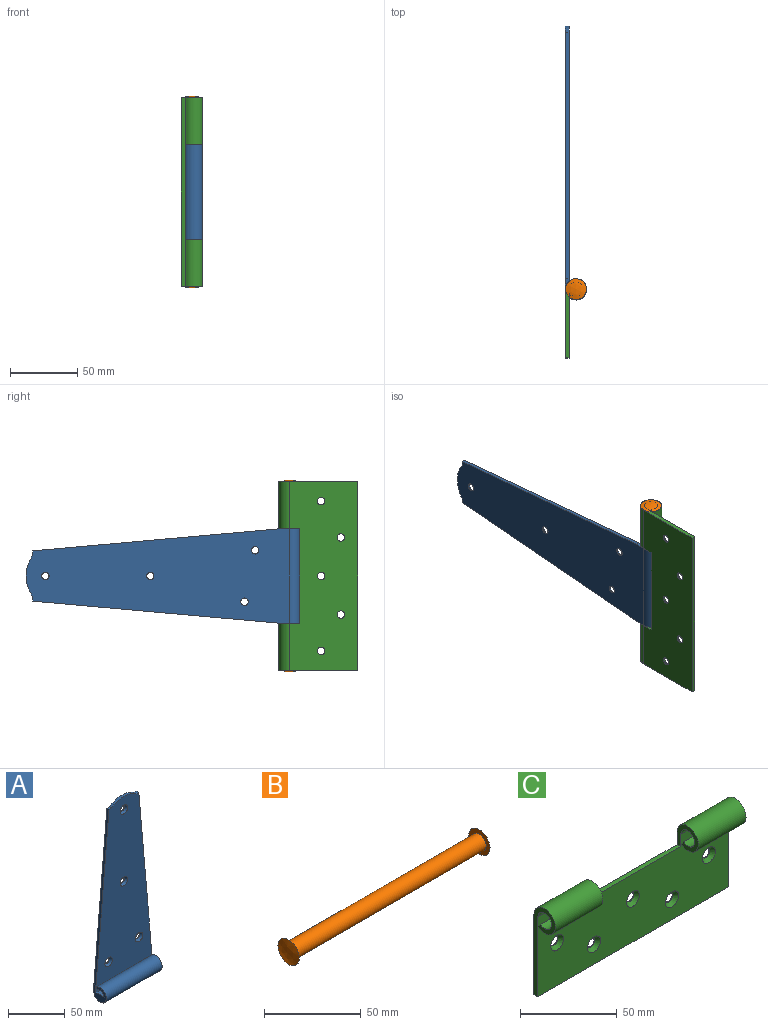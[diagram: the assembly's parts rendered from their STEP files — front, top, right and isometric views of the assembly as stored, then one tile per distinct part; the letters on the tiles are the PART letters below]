
ASSEMBLY  parts=3 mates=2
PART A: 21 faces, bbox 69.9x15.6x203.1 mm
  f0: cone r=4.76mm half-angle=41deg, axis (0,-1,0), area 72.6mm2, adj f7,f11
  f1: cone r=4.76mm half-angle=41deg, axis (0,-1,0), area 72.6mm2, adj f6,f11
  f2: cone r=4.76mm half-angle=41deg, axis (0,-1,0), area 72.6mm2, adj f5,f11
  f3: cone r=4.76mm half-angle=41deg, axis (0,-1,0), area 72.6mm2, adj f4,f11
  f4: cylinder r=2.74mm len=5.49mm, axis (0,1,0), area 5.9mm2, adj f3,f10
  f5: cylinder r=2.74mm len=5.49mm, axis (0,1,0), area 5.9mm2, adj f2,f10
  f6: cylinder r=2.74mm len=5.49mm, axis (0,1,0), area 5.9mm2, adj f1,f10
  f7: cylinder r=2.74mm len=5.49mm, axis (0,1,0), area 5.9mm2, adj f0,f10
  f8: cylinder r=4.96mm len=69.85mm, axis (-1,0,0), area 778.4mm2, adj f12,f13,f14,f15
  f9: cylinder r=7.8mm len=69.85mm, axis (-1,0,0), area 2934.7mm2, adj f10,f13,f14,f15
  f10: plane 195.26x69.85mm, normal (0,1,0), area 10328.3mm2, adj f4,f5,f6,f7,f9,f14,f15,f16
  f11: plane 195.26x69.85mm, normal (0,-1,0), area 10137.8mm2, adj f0,f1,f2,f3,f12,f14,f15,f16
  f12: plane 69.85x10.09mm, normal (0,0,1), area 704.9mm2, adj f8,f11,f14,f15
  f13: plane 69.85x2.21mm, normal (0,0.78,-0.63), area 198.2mm2, adj f8,f9,f14,f15
  f14: plane 15.6x15.6mm, normal (1,0,0), area 157mm2, adj f8,f9,f10,f11,f12,f13,f19
  f15: plane 15.6x15.6mm, normal (-1,0,0), area 157mm2, adj f8,f9,f10,f11,f12,f13,f20
  f16: cylinder r=25.9mm len=30.27mm, axis (0,-1,0), area 86.2mm2, adj f10,f11,f17,f18
  f17: plane 3.49x2.67mm, normal (0,0,1), area 9.3mm2, adj f10,f11,f16,f20
  f18: plane 3.49x2.67mm, normal (0,0,1), area 9.3mm2, adj f10,f11,f16,f19
  f19: plane 182.58x16.3mm, normal (1,0,0.09), area 488.9mm2, adj f10,f11,f14,f18
  f20: plane 182.58x16.3mm, normal (-1,0,0.09), area 488.9mm2, adj f10,f11,f15,f17
PART B: 5 faces, bbox 142.1x15.6x15.7 mm
  f0: sphere r=26.13mm, area 195.5mm2, adj f4
  f1: cylinder r=4.96mm len=139.7mm, axis (1,0,0), area 4354.5mm2, adj f3,f4
  f2: sphere r=26.13mm, area 195.5mm2, adj f3
  f3: plane 15.6x15.6mm, normal (-1,0,0), area 113.7mm2, adj f1,f2
  f4: plane 15.6x15.6mm, normal (1,0,0), area 113.7mm2, adj f0,f1
PART C: 26 faces, bbox 139.7x15.6x58.6 mm
  f0: cone r=4.76mm half-angle=41deg, axis (0,-1,0), area 72.6mm2, adj f9,f14
  f1: cone r=4.76mm half-angle=41deg, axis (0,-1,0), area 72.6mm2, adj f8,f14
  f2: cone r=4.76mm half-angle=41deg, axis (0,-1,0), area 72.6mm2, adj f7,f14
  f3: cone r=4.76mm half-angle=41deg, axis (0,-1,0), area 72.6mm2, adj f6,f14
  f4: cone r=4.76mm half-angle=41deg, axis (0,-1,0), area 72.6mm2, adj f5,f14
  f5: cylinder r=2.74mm len=5.49mm, axis (0,1,0), area 5.9mm2, adj f4,f15
  f6: cylinder r=2.74mm len=5.49mm, axis (0,1,0), area 5.9mm2, adj f3,f15
  f7: cylinder r=2.74mm len=5.49mm, axis (0,1,0), area 5.9mm2, adj f2,f15
  f8: cylinder r=2.74mm len=5.49mm, axis (0,1,0), area 5.9mm2, adj f1,f15
  f9: cylinder r=2.74mm len=5.49mm, axis (0,1,0), area 5.9mm2, adj f0,f15
  f10: cylinder r=4.96mm len=34.93mm, axis (-1,0,0), area 933.5mm2, adj f17,f19,f21,f24
  f11: cylinder r=4.96mm len=34.93mm, axis (-1,0,0), area 933.5mm2, adj f16,f18,f22,f23
  f12: cylinder r=7.8mm len=34.93mm, axis (-1,0,0), area 1467.4mm2, adj f15,f17,f21,f24
  f13: cylinder r=7.8mm len=34.93mm, axis (-1,0,0), area 1467.4mm2, adj f15,f16,f22,f23
  f14: plane 139.7x50.8mm, normal (0,-1,0), area 6195.8mm2, adj f0,f1,f2,f3,f4,f18,f19,f20
  f15: plane 139.7x50.8mm, normal (0,1,0), area 6433.9mm2, adj f5,f6,f7,f8,f9,f12,f13,f20
  f16: plane 34.93x2.21mm, normal (0,0.78,0.63), area 99.1mm2, adj f11,f13,f22,f23
  f17: plane 34.93x2.21mm, normal (0,0.78,0.63), area 99.1mm2, adj f10,f12,f21,f24
  f18: plane 34.93x0.17mm, normal (0,0,-1), area 5.9mm2, adj f11,f14,f22,f23
  f19: plane 34.93x0.17mm, normal (0,0,-1), area 5.9mm2, adj f10,f14,f21,f24
  f20: plane 139.7x2.67mm, normal (0,0,-1), area 372.6mm2, adj f14,f15,f21,f22
  f21: plane 58.6x15.6mm, normal (1,0,0), area 233mm2, adj f10,f12,f14,f15,f17,f19,f20
  f22: plane 58.6x15.6mm, normal (-1,0,0), area 233mm2, adj f11,f13,f14,f15,f16,f18,f20
  f23: plane 15.6x15.6mm, normal (1,0,0), area 118.3mm2, adj f11,f13,f14,f15,f16,f18,f25
  f24: plane 15.6x15.6mm, normal (-1,0,0), area 118.3mm2, adj f10,f12,f14,f15,f17,f19,f25
  f25: plane 69.85x2.67mm, normal (0,0,1), area 186.3mm2, adj f14,f15,f23,f24
PLACE A rot(axis=(-0.58,0.58,0.58),120deg) t=(193.02,36.35,109.6)mm
PLACE B rot(axis=(-0.58,0.58,0.58),120deg) t=(193.02,36.35,109.6)mm
PLACE C rot(axis=(-0.58,0.58,0.58),120deg) t=(193.02,36.35,109.6)mm
MATE fastened B.f1 <-> A.f8  axis (0,0,-1) through (185.22,36.35,109.6)mm
MATE revolute C.f10 <-> B.f1  axis (0,0,-1) through (185.22,36.35,39.75)mm
